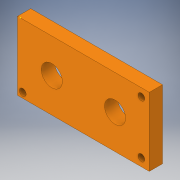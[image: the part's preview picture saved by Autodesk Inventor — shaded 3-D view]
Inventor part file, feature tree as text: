
AUTODESK INVENTOR PART (.ipt)
format: ipt  version: 2017 (Build 210142000, 142)  size: 177,152 bytes
history: native  units: in
note: dims shown in document units (in); Inventor stores cm internally (conversion verified against a paired STEP export)
features: sketch x12, extrude x11
ambient origin geometry x8: Origin, YZ Plane, XZ Plane, XY Plane, X Axis, Y Axis, Z Axis, Center Point
bodies: Solid1 (feature_tree)
feature tree (23):
  extrude  "Extrusion1"  Depth=1.3in
  sketch  "Sketch4"  dims[d2=0.25in d3=0.0in d14=0.2in d15=0.0in]
  extrude  "Extrusion4"  Depth=0.2in TaperAngle=0.0deg
  extrude  "Extrusion5"  Depth=0.65in
  extrude  "Extrusion6"  Depth=0.4in
  extrude  "Extrusion7"  Depth=0.3in TaperAngle=0.0deg
  extrude  "Extrusion9"  Depth=0.05in TaperAngle=0.0deg
  extrude  "Extrusion10"  Depth=0.13in
  extrude  "Extrusion11"  Depth=0.15in
  extrude  "Extrusion13"  Depth=0.15in
  extrude  "Extrusion14"  Depth=0.25in TaperAngle=0.0deg
  extrude  "Extrusion15"  Depth=0.1in
  sketch  "Sketch1"  dims[d0=2.3in d1=1.3in]
  sketch  "Sketch5"  dims[d16=0.4in d17=0.65in]
  sketch  "Sketch6"  dims[d18=0.6in d19=0.4in]
  sketch  "Sketch7"  dims[d20=1.05in d21=0.3in d22=0.0in]
  sketch  "Sketch8"  dims[d23=0.1in d24=0.0in d25=0.05in d26=0.0in]
  sketch  "Sketch10"  dims[d35=0.05in d36=0.0in d37=0.13in]
  sketch  "Sketch11"  dims[d38=0.13in d39=0.15in]
  sketch  "Sketch12"  dims[d40=0.15in d41=0.15in]
  sketch  "Sketch14"  dims[d42=0.15in d43=0.25in d44=0.0in]
  sketch  "Sketch15"  dims[d45=0.13in d46=0.1in]
  sketch  "Sketch16"  dims[d47=0.1in d48=0.25in d49=0.0in d55=0.65in d56=1.2in d57=0.4in d58=1.0in d59=0.0in d60=0.4in d61=1.0in d62=0.0in d63=2.0in d64=0.0in]
